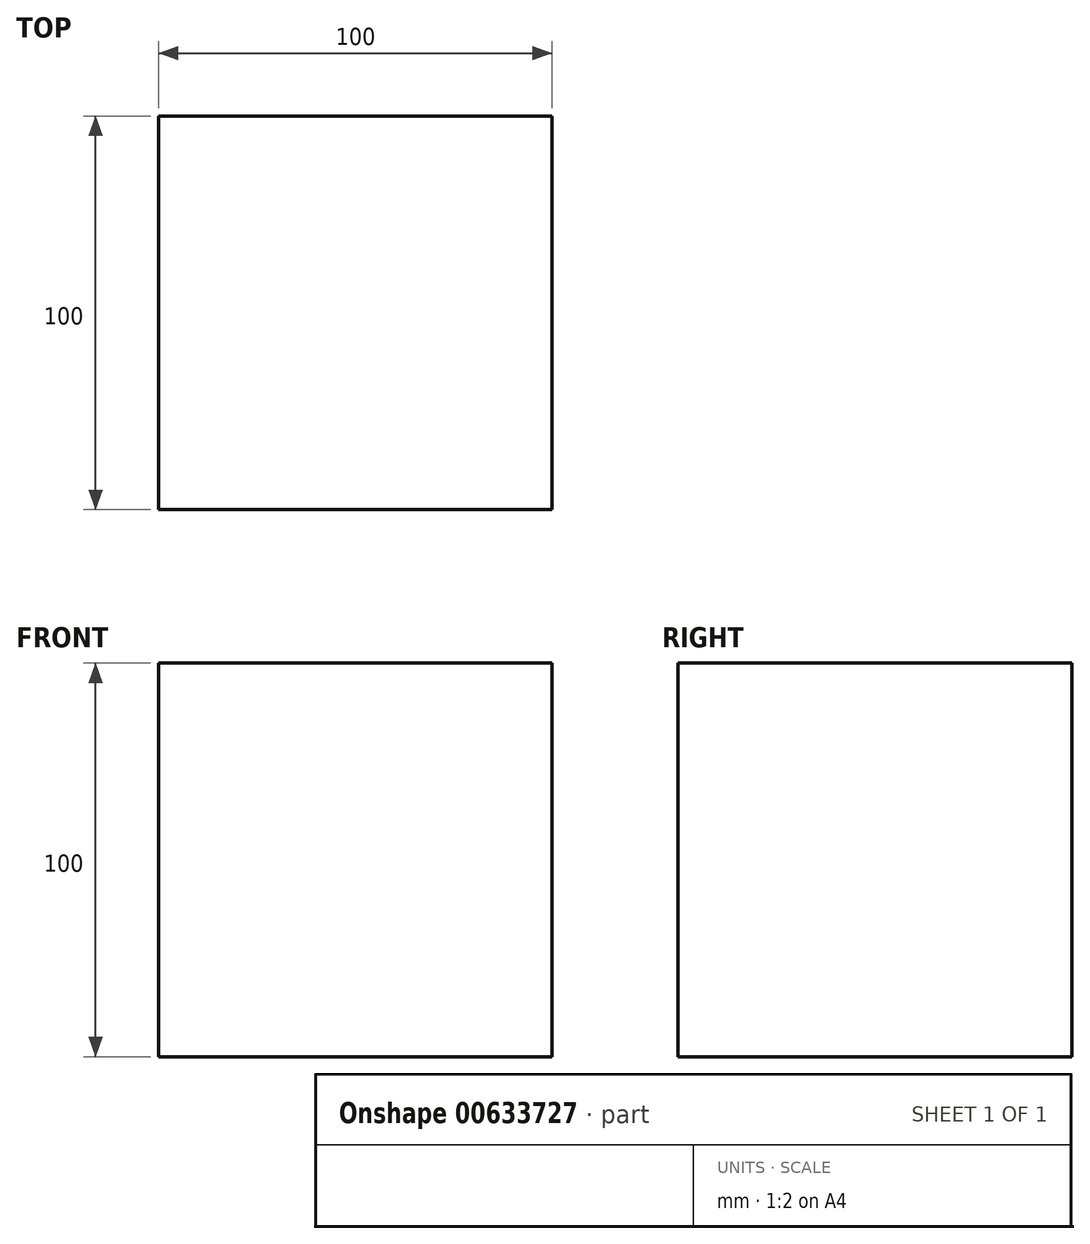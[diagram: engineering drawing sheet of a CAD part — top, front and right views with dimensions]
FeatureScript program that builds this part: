
annotation { "Feature Type Name" : "Feature", "Feature Type Description" : "" }
export const myFeature = defineFeature(function(context is Context, id is Id, definition is map)
    precondition{}
    {
        {
            var Q0;
            Q0=qCreatedBy(makeId("Top.planeOp"),FACE);
            var sketch = newSketch(context, id + "F0", { "sketchPlane" : qUnion([Q0])});
            skLineSegment(sketch, "E0.bottom", {"start": v(50, 50) * mm, "end": v(-50, 50) * mm});
            skLineSegment(sketch, "E0.top", {"start": v(50, -50) * mm, "end": v(-50, -50) * mm});
            skLineSegment(sketch, "E0.left", {"start": v(50, 50) * mm, "end": v(50, -50) * mm});
            skLineSegment(sketch, "E0.right", {"start": v(-50, 50) * mm, "end": v(-50, -50) * mm});
            skPoint(sketch, "E0.middle", {"position": v(0, 0) * mm});
            skSolve(sketch);
        }
        {
            var Q0;
            Q0=makeQuery(id+"F0.imprint","IMPRINT",FACE,{"disambiguationData":[TD([[makeQuery(id+"F0.imprint","IMPRINT",EDGE,{"derivedFrom":sQuery(id+"F0.wireOp",EDGE,"E0.bottom")}),1.0]])]});
            extrude(context, id + "F1", {"entities" : qUnion([Q0]), "depth" : 100 * mm, "offsetDistance" : 25 * mm});
        }
    });
